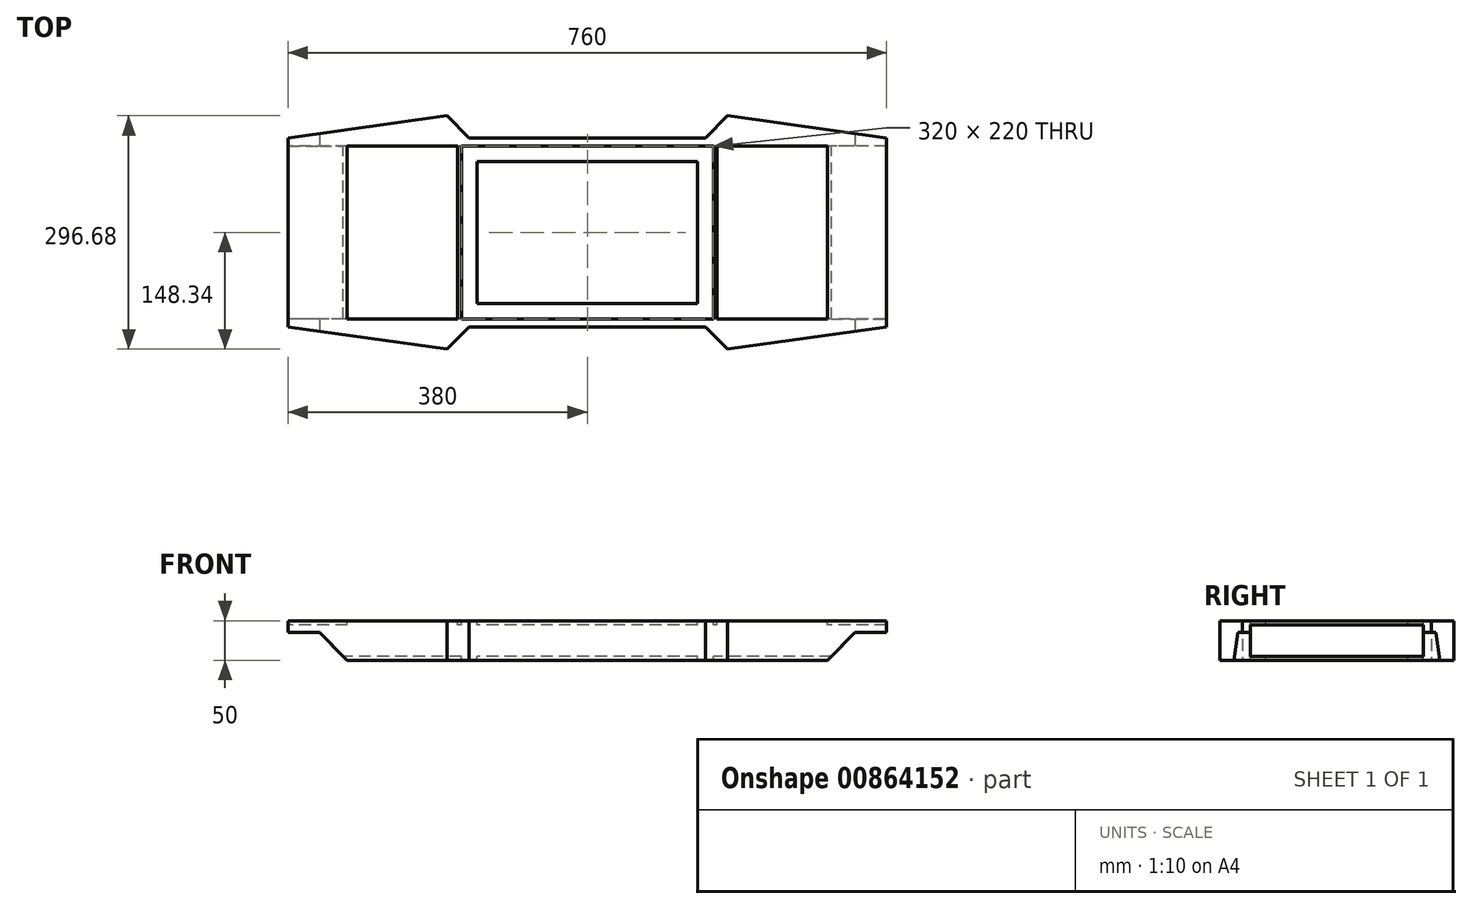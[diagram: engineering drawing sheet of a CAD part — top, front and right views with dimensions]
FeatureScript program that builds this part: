
annotation { "Feature Type Name" : "Feature", "Feature Type Description" : "" }
export const myFeature = defineFeature(function(context is Context, id is Id, definition is map)
    precondition{}
    {
        {
            var Q0;
            Q0=qCreatedBy(makeId("Top.planeOp"),FACE);
            var sketch = newSketch(context, id + "F0", { "sketchPlane" : qUnion([Q0])});
            skLineSegment(sketch, "E0", {"start": v(-380, 120) * mm, "end": v(-380, -120) * mm});
            skLineSegment(sketch, "E1", {"start": v(380, 120) * mm, "end": v(380, -120) * mm});
            skLineSegment(sketch, "E2", {"start": v(150, -120) * mm, "end": v(-150, -120) * mm});
            skLineSegment(sketch, "E3", {"start": v(-150, 120) * mm, "end": v(150, 120) * mm});
            skLineSegment(sketch, "E4", {"start": v(-160, 110) * mm, "end": v(160, 110) * mm, "construction": true});
            skLineSegment(sketch, "E5", {"start": v(160, 110) * mm, "end": v(160, -110) * mm, "construction": true});
            skLineSegment(sketch, "E6", {"start": v(160, -110) * mm, "end": v(-160, -110) * mm, "construction": true});
            skLineSegment(sketch, "E7", {"start": v(-160, -110) * mm, "end": v(-160, 110) * mm, "construction": true});
            skLineSegment(sketch, "E8.0", {"start": v(-150, -110) * mm, "end": v(-150, 110) * mm, "construction": true});
            skLineSegment(sketch, "E9.0", {"start": v(150, 110) * mm, "end": v(150, -110) * mm, "construction": true});
            skLineSegment(sketch, "E10", {"start": v(-150, -110) * mm, "end": v(-150, -120) * mm, "construction": true});
            skLineSegment(sketch, "E11", {"start": v(-150, 110) * mm, "end": v(-150, 120) * mm, "construction": true});
            skLineSegment(sketch, "E12", {"start": v(-150, 120) * mm, "end": v(-178.34, 148.34) * mm});
            skLineSegment(sketch, "E13", {"start": v(-380, 120) * mm, "end": v(-178.34, 148.34) * mm});
            skPoint(sketch, "E14.endSnap0", {"position": v(0, 110) * mm});
            skLineSegment(sketch, "E15.MirrorCS", {"start": v(150, 120) * mm, "end": v(178.34, 148.34) * mm});
            skLineSegment(sketch, "E16.MirrorCS", {"start": v(380, 120) * mm, "end": v(178.34, 148.34) * mm});
            skLineSegment(sketch, "E17.MirrorCS", {"start": v(-150, -120) * mm, "end": v(-178.34, -148.34) * mm, "construction": true});
            skLineSegment(sketch, "E18.MirrorCS", {"start": v(-380, -120) * mm, "end": v(-178.34, -148.34) * mm});
            skLineSegment(sketch, "E19.MirrorCS", {"start": v(150, -120) * mm, "end": v(178.34, -148.34) * mm});
            skLineSegment(sketch, "E20.MirrorCS", {"start": v(-150, -120) * mm, "end": v(-178.34, -148.34) * mm});
            skLineSegment(sketch, "E21.MirrorCS", {"start": v(380, -120) * mm, "end": v(178.34, -148.34) * mm});
            skSolve(sketch);
        }
        {
            var Q0;
            Q0=makeQuery(id+"F0.imprint","IMPRINT",FACE,{"disambiguationData":[TD([[makeQuery(id+"F0.imprint","IMPRINT",EDGE,{"derivedFrom":sQuery(id+"F0.wireOp",EDGE,"E0")}),1.0]])]});
            extrude(context, id + "F1", {"entities" : qUnion([Q0]), "depth" : 50 * mm, "offsetDistance" : 25 * mm});
        }
        {
            var Q0;
            Q0=makeQuery(id+"F1.opExtrude","SWEPT_FACE",FACE,{"disambiguationData":[OSD([sQuery(id+"F0.wireOp",EDGE,"E2")])]});
            var sketch = newSketch(context, id + "F2", { "sketchPlane" : qUnion([Q0])});
            skLineSegment(sketch, "E22", {"start": v(-380, 35) * mm, "end": v(-340, 35) * mm});
            skLineSegment(sketch, "E23", {"start": v(-340, 35) * mm, "end": v(-305, 0) * mm});
            skLineSegment(sketch, "E24", {"start": v(-380, 35) * mm, "end": v(-380, 0) * mm});
            skLineSegment(sketch, "E25", {"start": v(-380, 0) * mm, "end": v(-305, 0) * mm});
            skLineSegment(sketch, "E26.MirrorCS", {"start": v(380, 0) * mm, "end": v(305, 0) * mm});
            skLineSegment(sketch, "E27.MirrorCS", {"start": v(380, 35) * mm, "end": v(380, 0) * mm});
            skLineSegment(sketch, "E28.MirrorCS", {"start": v(380, 35) * mm, "end": v(340, 35) * mm});
            skLineSegment(sketch, "E29.MirrorCS", {"start": v(340, 35) * mm, "end": v(305, 0) * mm});
            skSolve(sketch);
        }
        {
            var Q0;
            Q0=makeQuery(id+"F1.opExtrude","SWEPT_FACE",FACE,{"disambiguationData":[OSD([sQuery(id+"F0.wireOp",EDGE,"E0")])]});
            var sketch = newSketch(context, id + "F3", { "sketchPlane" : qUnion([Q0])});
            skLineSegment(sketch, "E30.0", {"start": v(-110, 45) * mm, "end": v(110, 45) * mm});
            skLineSegment(sketch, "E31.0", {"start": v(-110, 5) * mm, "end": v(110, 5) * mm});
            skLineSegment(sketch, "E32.0", {"start": v(-110, 5) * mm, "end": v(-110, 45) * mm});
            skLineSegment(sketch, "E33.0", {"start": v(110, 45) * mm, "end": v(110, 5) * mm});
            skSolve(sketch);
        }
        {
            var Q0;
            Q0=makeQuery(id+"F3.imprint","IMPRINT",FACE,{"disambiguationData":[TD([[makeQuery(id+"F3.imprint","IMPRINT",EDGE,{"derivedFrom":sQuery(id+"F3.wireOp",EDGE,"E30.0")}),-1.0]])]});
            extrude(context, id + "F4", {"entities" : qUnion([Q0]), "operationType" : NewBodyOperationType.REMOVE, "oppositeDirection" : true, "depth" : 760 * mm, "offsetDistance" : 25 * mm});
        }
        {
            var Q0;
            Q0=makeQuery(id+"F2.imprint","IMPRINT",FACE,{"disambiguationData":[TD([[makeQuery(id+"F2.imprint","IMPRINT",EDGE,{"derivedFrom":sQuery(id+"F2.wireOp",EDGE,"E26.MirrorCS")}),-1.0]])]});
            var Q1;
            Q1=makeQuery(id+"F2.imprint","IMPRINT",FACE,{"disambiguationData":[TD([[makeQuery(id+"F2.imprint","IMPRINT",EDGE,{"derivedFrom":sQuery(id+"F2.wireOp",EDGE,"E22")}),-1.0]])]});
            extrude(context, id + "F5", {"entities" : qUnion([Q0, Q1]), "operationType" : NewBodyOperationType.REMOVE, "oppositeDirection" : true, "depth" : 240 * mm, "offsetDistance" : 25 * mm});
        }
        {
            var Q0;
            Q0=makeQuery(id+"F1.opExtrude","CAP_FACE",FACE,{"disambiguationData":[OSD([sQuery(id+"F0.wireOp",EDGE,"E0"),sQuery(id+"F0.wireOp",EDGE,"E1"),sQuery(id+"F0.wireOp",EDGE,"E2"),sQuery(id+"F0.wireOp",EDGE,"E3")])],"isStart":false});
            var sketch = newSketch(context, id + "F6", { "sketchPlane" : qUnion([Q0])});
            skLineSegment(sketch, "E34", {"start": v(-140, 90) * mm, "end": v(140, 90) * mm});
            skLineSegment(sketch, "E35", {"start": v(140, 90) * mm, "end": v(140, -90) * mm});
            skLineSegment(sketch, "E36", {"start": v(140, -90) * mm, "end": v(-140, -90) * mm});
            skLineSegment(sketch, "E37", {"start": v(-140, -90) * mm, "end": v(-140, 90) * mm});
            skLineSegment(sketch, "E38", {"start": v(160, 110) * mm, "end": v(160, -110) * mm});
            skLineSegment(sketch, "E39", {"start": v(-160, 110) * mm, "end": v(-160, -110) * mm});
            skLineSegment(sketch, "E40", {"start": v(-160, 110) * mm, "end": v(160, 110) * mm});
            skLineSegment(sketch, "E41", {"start": v(160, -110) * mm, "end": v(-160, -110) * mm});
            skSolve(sketch);
        }
        {
            var Q0;
            Q0=qSketchRegion(id+"F6",true);
            extrude(context, id + "F7", {"entities" : qUnion([Q0]), "operationType" : NewBodyOperationType.REMOVE, "oppositeDirection" : true, "depth" : 50 * mm, "offsetDistance" : 25 * mm});
        }
        {
            var Q0;
            Q0 = qSketchRegion(id + "F2", true);
            extrude(context, id + "F8", {"entities" : qUnion([Q0]), "operationType" : NewBodyOperationType.REMOVE, "endBound" : BoundingType.SYMMETRIC, "oppositeDirection" : true, "depth" : 871.86 * mm, "offsetDistance" : 25 * mm});
        }
        {
            var Q0;
            {var subQ0=sQuery(id+"F0.wireOp",EDGE,"E18.MirrorCS");var subQ1=sQuery(id+"F0.wireOp",EDGE,"E16.MirrorCS");var subQ2=sQuery(id+"F0.wireOp",EDGE,"E15.MirrorCS");var subQ3=sQuery(id+"F0.wireOp",EDGE,"E13");var subQ4=sQuery(id+"F0.wireOp",EDGE,"E12");var subQ5=sQuery(id+"F0.wireOp",EDGE,"E19.MirrorCS");var subQ6=sQuery(id+"F0.wireOp",EDGE,"E0");var subQ7=sQuery(id+"F0.wireOp",EDGE,"E3");var subQ8=sQuery(id+"F0.wireOp",EDGE,"E1");var subQ9=sQuery(id+"F0.wireOp",EDGE,"E2");var subQ10=sQuery(id+"F0.wireOp",EDGE,"E20.MirrorCS");var subQ11=sQuery(id+"F0.wireOp",EDGE,"E21.MirrorCS");Q0=makeQuery(id+"F7.boolean.opBoolean","SPLIT",FACE,{"disambiguationData":[TD([makeQuery(id+"F1.opExtrude","SWEPT_FACE",FACE,{"disambiguationData":[OSD([subQ6])]})])],"derivedFrom":makeQuery(id+"F1.opExtrude","CAP_FACE",FACE,{"disambiguationData":[OSD([subQ6,subQ8,subQ9,subQ7,subQ4,subQ3,subQ2,subQ1,subQ0,subQ5,subQ10,subQ11])],"isStart":false})});}
            var sketch = newSketch(context, id + "F9", { "sketchPlane" : qUnion([Q0])});
            skLineSegment(sketch, "E42", {"start": v(-165, -110) * mm, "end": v(-305, -110) * mm});
            skLineSegment(sketch, "E43", {"start": v(-305, -110) * mm, "end": v(-305, 110) * mm});
            skLineSegment(sketch, "E44", {"start": v(-305, 110) * mm, "end": v(-165, 110) * mm});
            skLineSegment(sketch, "E45.0", {"start": v(-165, 110) * mm, "end": v(-165, -110) * mm});
            skLineSegment(sketch, "E46", {"start": v(0, 0) * mm, "end": v(0, 58.76) * mm});
            skLineSegment(sketch, "E47.MirrorCS", {"start": v(165, 110) * mm, "end": v(165, -110) * mm});
            skLineSegment(sketch, "E48.MirrorCS", {"start": v(165, -110) * mm, "end": v(305, -110) * mm});
            skLineSegment(sketch, "E49.MirrorCS", {"start": v(305, -110) * mm, "end": v(305, 110) * mm});
            skLineSegment(sketch, "E50.MirrorCS", {"start": v(305, 110) * mm, "end": v(165, 110) * mm});
            skSolve(sketch);
        }
        {
            var Q0;
            Q0=makeQuery(id+"F9.imprint","IMPRINT",FACE,{"disambiguationData":[TD([[makeQuery(id+"F9.imprint","IMPRINT",EDGE,{"derivedFrom":sQuery(id+"F9.wireOp",EDGE,"E42")}),-1.0]])]});
            var Q1;
            Q1=makeQuery(id+"F9.imprint","IMPRINT",FACE,{"disambiguationData":[TD([[makeQuery(id+"F9.imprint","IMPRINT",EDGE,{"derivedFrom":sQuery(id+"F9.wireOp",EDGE,"E47.MirrorCS")}),1.0]])]});
            extrude(context, id + "F10", {"entities" : qUnion([Q0, Q1]), "operationType" : NewBodyOperationType.REMOVE, "oppositeDirection" : true, "depth" : 10 * mm, "offsetDistance" : 25 * mm});
        }
    });
